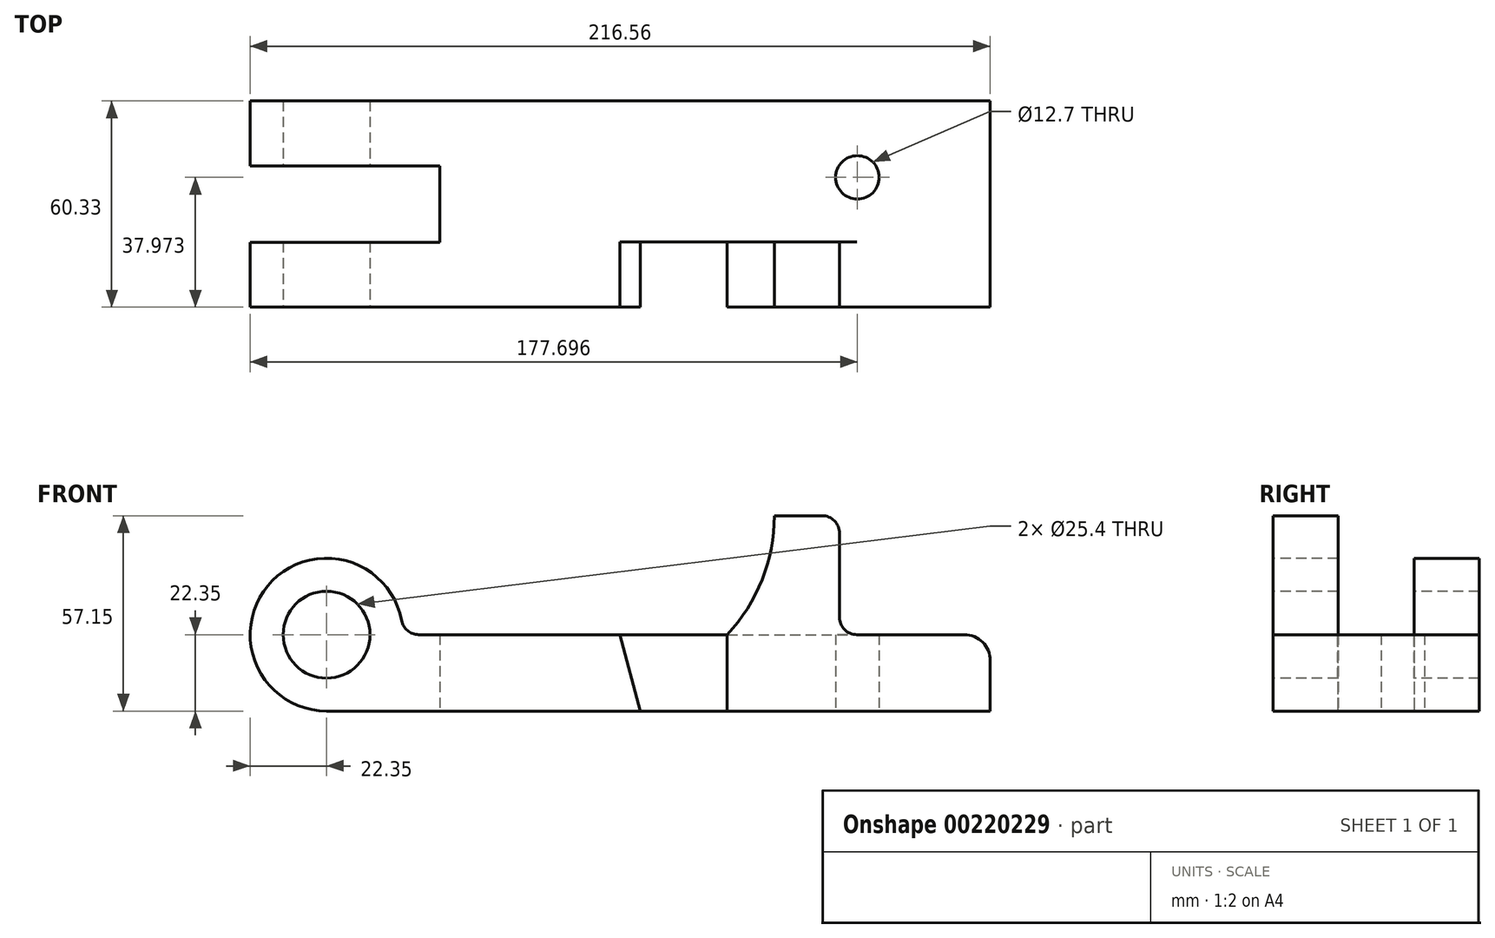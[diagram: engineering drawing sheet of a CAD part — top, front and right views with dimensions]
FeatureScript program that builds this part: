
annotation { "Feature Type Name" : "Feature", "Feature Type Description" : "" }
export const myFeature = defineFeature(function(context is Context, id is Id, definition is map)
    precondition{}
    {
        {
            var Q0;
            Q0=qCreatedBy(makeId("Front.planeOp"),FACE);
            var sketch = newSketch(context, id + "F0", { "sketchPlane" : qUnion([Q0])});
            skCircle(sketch, "E0", {"center": v(0, 0) * mm, "radius": 12.7 * mm});
            skArc(sketch, "E1", {"start": v(-22.35, 0) * mm, "mid": v(-15.8, -15.8) * mm, "end": v(0, -22.35) * mm});
            skLineSegment(sketch, "E2", {"start": v(0, -22.35) * mm, "end": v(194.2, -22.35) * mm});
            skLineSegment(sketch, "E3", {"start": v(194.2, -22.35) * mm, "end": v(194.2, 0) * mm});
            skLineSegment(sketch, "E4", {"start": v(194.2, 0) * mm, "end": v(150.09, 0) * mm});
            skLineSegment(sketch, "E5", {"start": v(150.09, 0) * mm, "end": v(150.09, 34.8) * mm});
            skLineSegment(sketch, "E6", {"start": v(150.09, 34.8) * mm, "end": v(131.04, 34.8) * mm});
            skLineSegment(sketch, "E7", {"start": v(117.25, 0) * mm, "end": v(85.85, 0) * mm});
            skArc(sketch, "E8", {"start": v(131.04, 34.8) * mm, "mid": v(127.46, 16.08) * mm, "end": v(117.25, 0) * mm});
            skLineSegment(sketch, "E9", {"start": v(117.25, 0) * mm, "end": v(117.25, -22.35) * mm});
            skPoint(sketch, "E10", {"position": v(91.85, -22.35) * mm});
            skPoint(sketch, "E11", {"position": v(85.85, 0) * mm});
            skLineSegment(sketch, "E12", {"start": v(85.85, 0) * mm, "end": v(91.85, -22.35) * mm});
            skLineSegment(sketch, "E13", {"start": v(85.85, 0) * mm, "end": v(22.35, 0) * mm});
            skArc(sketch, "E14", {"start": v(-22.35, 0) * mm, "mid": v(0, 22.35) * mm, "end": v(22.35, 0) * mm});
            skLineSegment(sketch, "E15", {"start": v(150.09, 0) * mm, "end": v(150.09, -22.35) * mm});
            skLineSegment(sketch, "E16", {"start": v(150.09, 0) * mm, "end": v(117.25, 0) * mm});
            skSolve(sketch);
        }
        {
            var Q0;
            Q0=makeQuery(id+"F0.imprint","IMPRINT",FACE,{"disambiguationData":[TD([[makeQuery(id+"F0.imprint","IMPRINT",EDGE,{"derivedFrom":sQuery(id+"F0.wireOp",EDGE,"E0")}),-1.0]])]});
            var Q1;
            Q1=makeQuery(id+"F0.imprint","IMPRINT",FACE,{"disambiguationData":[TD([[makeQuery(id+"F0.imprint","IMPRINT",EDGE,{"derivedFrom":sQuery(id+"F0.wireOp",EDGE,"E7")}),1.0]])]});
            var Q2;
            {var subQ0=sQuery(id+"F0.wireOp",EDGE,"E3");Q2=makeQuery(id+"F0.imprint","IMPRINT",FACE,{"disambiguationData":[TD([[makeQuery(id+"F0.imprint","IMPRINT",EDGE,{"derivedFrom":subQ0}),1.0]])]});}
            var Q3;
            Q3=makeQuery(id+"F0.imprint","IMPRINT",FACE,{"disambiguationData":[TD([[makeQuery(id+"F0.imprint","IMPRINT",EDGE,{"derivedFrom":sQuery(id+"F0.wireOp",EDGE,"E5")}),1.0]])]});
            var Q4;
            {var subQ0=sQuery(id+"F0.wireOp",EDGE,"E9");Q4=makeQuery(id+"F0.imprint","IMPRINT",FACE,{"disambiguationData":[TD([[makeQuery(id+"F0.imprint","IMPRINT",EDGE,{"derivedFrom":subQ0}),1.0]])]});}
            extrude(context, id + "F1", {"entities" : qUnion([Q0, Q1, Q2, Q3, Q4]), "oppositeDirection" : true, "depth" : 60.32 * mm});
        }
        {
            var Q0;
            Q0=makeQuery(id+"F0.imprint","IMPRINT",FACE,{"disambiguationData":[TD([[makeQuery(id+"F0.imprint","IMPRINT",EDGE,{"derivedFrom":sQuery(id+"F0.wireOp",EDGE,"E7")}),1.0]])]});
            extrude(context, id + "F2", {"entities" : qUnion([Q0]), "operationType" : NewBodyOperationType.REMOVE, "oppositeDirection" : true, "depth" : 19.05 * mm});
        }
        {
            var Q0;
            Q0=makeQuery(id+"F1.opExtrude","SWEPT_FACE",FACE,{"disambiguationData":[OSD([sQuery(id+"F0.wireOp",EDGE,"E2")])]});
            var sketch = newSketch(context, id + "F3", { "sketchPlane" : qUnion([Q0])});
            skLineSegment(sketch, "E17.bottom", {"start": v(33.14, -19) * mm, "end": v(-55.29, -19) * mm});
            skLineSegment(sketch, "E17.top", {"start": v(33.14, -41.33) * mm, "end": v(-55.29, -41.33) * mm});
            skLineSegment(sketch, "E17.left", {"start": v(33.14, -19) * mm, "end": v(33.14, -41.33) * mm});
            skLineSegment(sketch, "E17.right", {"start": v(-55.29, -19) * mm, "end": v(-55.29, -41.33) * mm});
            skPoint(sketch, "E17.middle", {"position": v(-11.07, -30.16) * mm});
            skPoint(sketch, "E17.middle.positionSnap0", {"position": v(0, -30.16) * mm});
            skPoint(sketch, "E17.centerSnap0", {"position": v(0, -30.16) * mm});
            skCircle(sketch, "E18", {"center": v(155.35, -37.97) * mm, "radius": 6.35 * mm});
            skSolve(sketch);
        }
        {
            var Q0;
            {var subQ0=sQuery(id+"F3.wireOp",EDGE,"E17.left");Q0=makeQuery(id+"F3.imprint","IMPRINT",FACE,{"disambiguationData":[TD([[makeQuery(id+"F3.imprint","IMPRINT",EDGE,{"derivedFrom":subQ0}),-1.0]])]});}
            var Q1;
            {var subQ0=sQuery(id+"F3.wireOp",EDGE,"E17.right");Q1=makeQuery(id+"F3.imprint","IMPRINT",FACE,{"disambiguationData":[TD([[makeQuery(id+"F3.imprint","IMPRINT",EDGE,{"derivedFrom":subQ0}),1.0]])]});}
            var Q2;
            Q2=makeQuery(id+"F3.imprint","IMPRINT",FACE,{"disambiguationData":[TD([[makeQuery(id+"F3.imprint","IMPRINT",EDGE,{"derivedFrom":sQuery(id+"F3.wireOp",EDGE,"E18")}),1.0]])]});
            extrude(context, id + "F4", {"entities" : qUnion([Q0, Q1, Q2]), "operationType" : NewBodyOperationType.REMOVE, "endBound" : BoundingType.THROUGH_ALL, "oppositeDirection" : true, "depth" : 25.4 * mm});
        }
        {
            var Q0;
            Q0=makeQuery(id+"F1.opExtrude","CAP_FACE",FACE,{"disambiguationData":[OSD([sQuery(id+"F0.wireOp",EDGE,"E0"),sQuery(id+"F0.wireOp",EDGE,"E1"),sQuery(id+"F0.wireOp",EDGE,"E2"),sQuery(id+"F0.wireOp",EDGE,"E3"),sQuery(id+"F0.wireOp",EDGE,"E4"),sQuery(id+"F0.wireOp",EDGE,"E5"),sQuery(id+"F0.wireOp",EDGE,"E6"),sQuery(id+"F0.wireOp",EDGE,"E7"),sQuery(id+"F0.wireOp",EDGE,"E8"),sQuery(id+"F0.wireOp",EDGE,"E13"),sQuery(id+"F0.wireOp",EDGE,"E14")])],"isStart":false});
            var sketch = newSketch(context, id + "F5", { "sketchPlane" : qUnion([Q0])});
            skLineSegment(sketch, "E19.0.0", {"start": v(-117.25, 0) * mm, "end": v(-150.09, 0) * mm});
            skLineSegment(sketch, "E19.0.1", {"start": v(-150.09, 0) * mm, "end": v(-150.09, 34.8) * mm});
            skLineSegment(sketch, "E19.0.2", {"start": v(-150.09, 34.8) * mm, "end": v(-131.04, 34.8) * mm});
            skArc(sketch, "E19.0.3", {"start": v(-131.04, 34.8) * mm, "mid": v(-127.46, 16.08) * mm, "end": v(-117.25, 0) * mm});
            skSolve(sketch);
        }
        {
            var Q0;
            Q0 = qSketchRegion(id + "F5", true);
            extrude(context, id + "F6", {"entities" : qUnion([Q0]), "operationType" : NewBodyOperationType.REMOVE, "oppositeDirection" : true, "depth" : 41.27 * mm});
        }
        {
            var Q0;
            {var subQ0=sQuery(id+"F0.wireOp",EDGE,"E14");var subQ1=sQuery(id+"F0.wireOp",EDGE,"E13");Q0=makeQuery(id+"F4.boolean.opBoolean","SPLIT",EDGE,{"disambiguationData":[TD([makeQuery(id+"F4.opExtrude","SWEPT_FACE",FACE,{"disambiguationData":[OSD([sQuery(id+"F3.wireOp",EDGE,"E17.bottom")])]})])],"derivedFrom":makeQuery(id+"F1.opExtrude","SWEPT_EDGE",EDGE,{"disambiguationData":[OSD([subQ1,subQ0])]})});}
            var Q1;
            {var subQ0=sQuery(id+"F0.wireOp",EDGE,"E6");var subQ1=sQuery(id+"F0.wireOp",EDGE,"E5");Q1=makeQuery(id+"F4.boolean.opBoolean","SPLIT",EDGE,{"disambiguationData":[TD([makeQuery(id+"F1.opExtrude","CAP_FACE",FACE,{"disambiguationData":[OSD([sQuery(id+"F0.wireOp",EDGE,"E0"),sQuery(id+"F0.wireOp",EDGE,"E1"),sQuery(id+"F0.wireOp",EDGE,"E2"),sQuery(id+"F0.wireOp",EDGE,"E3"),sQuery(id+"F0.wireOp",EDGE,"E4"),subQ1,subQ0,sQuery(id+"F0.wireOp",EDGE,"E7"),sQuery(id+"F0.wireOp",EDGE,"E8"),sQuery(id+"F0.wireOp",EDGE,"E13"),sQuery(id+"F0.wireOp",EDGE,"E14")])],"isStart":true})])],"derivedFrom":makeQuery(id+"F1.opExtrude","SWEPT_EDGE",EDGE,{"disambiguationData":[OSD([subQ1,subQ0])]})});}
            var Q2;
            {var subQ0=sQuery(id+"F0.wireOp",EDGE,"E5");var subQ1=sQuery(id+"F0.wireOp",EDGE,"E4");Q2=makeQuery(id+"F4.boolean.opBoolean","SPLIT",EDGE,{"disambiguationData":[TD([makeQuery(id+"F1.opExtrude","CAP_FACE",FACE,{"disambiguationData":[OSD([sQuery(id+"F0.wireOp",EDGE,"E0"),sQuery(id+"F0.wireOp",EDGE,"E1"),sQuery(id+"F0.wireOp",EDGE,"E2"),sQuery(id+"F0.wireOp",EDGE,"E3"),subQ1,subQ0,sQuery(id+"F0.wireOp",EDGE,"E6"),sQuery(id+"F0.wireOp",EDGE,"E7"),sQuery(id+"F0.wireOp",EDGE,"E8"),sQuery(id+"F0.wireOp",EDGE,"E13"),sQuery(id+"F0.wireOp",EDGE,"E14")])],"isStart":true})])],"derivedFrom":makeQuery(id+"F1.opExtrude","SWEPT_EDGE",EDGE,{"disambiguationData":[OSD([subQ1,subQ0,sQuery(id+"F0.wireOp",EDGE,"E15"),sQuery(id+"F0.wireOp",EDGE,"E16")])]})});}
            var Q3;
            {var subQ0=sQuery(id+"F0.wireOp",EDGE,"E14");var subQ1=sQuery(id+"F0.wireOp",EDGE,"E13");Q3=makeQuery(id+"F4.boolean.opBoolean","SPLIT",EDGE,{"disambiguationData":[TD([makeQuery(id+"F4.opExtrude","SWEPT_FACE",FACE,{"disambiguationData":[OSD([sQuery(id+"F3.wireOp",EDGE,"E17.top")])]})])],"derivedFrom":makeQuery(id+"F1.opExtrude","SWEPT_EDGE",EDGE,{"disambiguationData":[OSD([subQ1,subQ0])]})});}
            fillet(context, id + "F7", {"entities" : qUnion([Q0, Q1, Q2, Q3]), "radius" : 5.08 * mm, "tangentPropagation" : true, "allowEdgeOverflow" : false});
        }
        {
            var Q0;
            Q0=makeQuery(id+"F1.opExtrude","SWEPT_EDGE",EDGE,{"disambiguationData":[OSD([sQuery(id+"F0.wireOp",EDGE,"E3"),sQuery(id+"F0.wireOp",EDGE,"E4")])]});
            fillet(context, id + "F8", {"entities" : qUnion([Q0]), "radius" : 7.62 * mm, "tangentPropagation" : true, "allowEdgeOverflow" : false});
        }
    });
